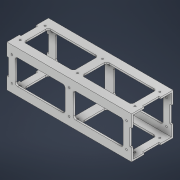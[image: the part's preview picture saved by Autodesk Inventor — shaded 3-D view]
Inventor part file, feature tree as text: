
AUTODESK INVENTOR PART (.ipt)
format: ipt  version: 2022 (Build 260153000, 153)  size: 380,416 bytes
history: native  units: in
note: dims shown in document units (in); Inventor stores cm internally (conversion verified against a paired STEP export)
features: extrude x7, sketch x5, fillet x1
ambient origin geometry x8: Origin, YZ Plane, XZ Plane, XY Plane, X Axis, Y Axis, Z Axis, Center Point
bodies: Solid1 (feature_tree)
feature tree (13):
  extrude  "Extrusion1"  Depth=1.9685in
  extrude  "Extrusion2"  Depth=1.811in
  extrude  "Extrusion3"  Depth=0.7874in
  extrude  "Extrusion4"  Depth=0.7874in
  extrude  "Extrusion5"  Depth=0.0787in TaperAngle=0.0deg
  sketch  "Sketch19"  dims[d7=0.7874in d8=0.7874in]
  extrude  "Extrusion14"  Depth=0.7874in
  extrude  "Extrusion15"  Depth=0.7874in
  fillet  "Fillet1"  Radius=0.7874in
  sketch  "Sketch1"  dims[d0=1.9685in d1=1.9685in]
  sketch  "Sketch2"  dims[d2=1.811in d3=1.811in]
  sketch  "Sketch3"  dims[d4=5.9055in d5=0.0in d6=0.7874in]
  sketch  "Sketch21"  dims[d9=0.7874in d10=0.0787in d11=0.0in d12=0.7874in d13=0.7874in d14=0.7874in d15=0.7874in d16=0.0787in d17=0.0in d19=2.3622in d20=1.1811in d21=2.3622in d22=1.1811in d23=0.0787in d24=0.0in d26=1.9685in d27=2.3622in d28=1.1811in d29=2.3622in d30=1.1811in d31=0.0787in d32=0.0in d75=0.0787in d76=0.0in d77=1.5748in d78=1.5748in d79=0.0787in d80=0.2362in d81=0.3937in d82=0.0787in d83=0.2362in d84=0.3937in d85=0.0787in d86=0.2362in d87=0.3937in d88=0.0787in d89=0.2362in d90=0.3937in d91=0.0787in d92=0.2362in d93=0.3937in d94=0.0787in d95=0.2362in d96=0.3937in d97=0.0787in d98=0.3937in d99=0.2362in d100=0.0787in d101=0.2362in d102=0.3937in d103=0.0in d104=0.0in d105=0.0787in d106=0.3937in d107=0.1969in d108=0.0787in d109=0.3937in d110=0.1969in d111=0.0787in d112=0.1969in d113=0.3937in d114=0.0787in d115=0.3937in d116=0.1969in d117=1.5748in d118=1.5748in d119=0.1181in d25=0.0197in]
